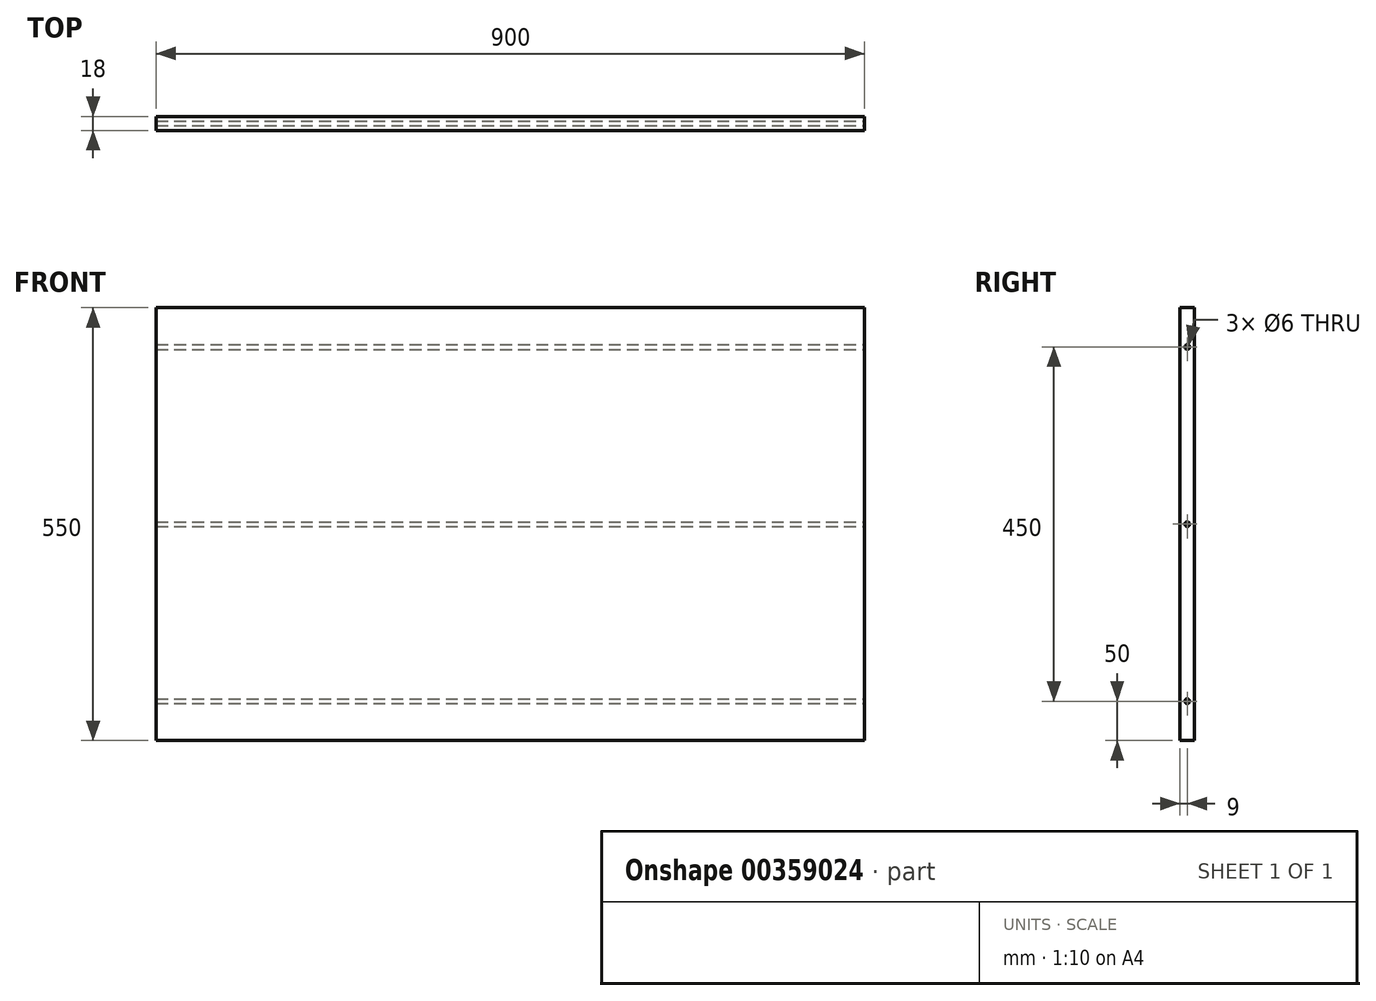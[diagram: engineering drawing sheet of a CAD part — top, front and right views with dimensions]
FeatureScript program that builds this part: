
annotation { "Feature Type Name" : "Feature", "Feature Type Description" : "" }
export const myFeature = defineFeature(function(context is Context, id is Id, definition is map)
    precondition{}
    {
        {
            var Q0;
            Q0=qCreatedBy(makeId("Front.planeOp"),FACE);
            var sketch = newSketch(context, id + "F0", { "sketchPlane" : qUnion([Q0])});
            skLineSegment(sketch, "E0.bottom", {"start": v(0, 0) * mm, "end": v(900, 0) * mm});
            skLineSegment(sketch, "E0.top", {"start": v(0, 550) * mm, "end": v(900, 550) * mm});
            skLineSegment(sketch, "E0.left", {"start": v(0, 0) * mm, "end": v(0, 550) * mm});
            skLineSegment(sketch, "E0.right", {"start": v(900, 0) * mm, "end": v(900, 550) * mm});
            skSolve(sketch);
        }
        {
            var Q0;
            Q0=makeQuery(id+"F0.imprint","IMPRINT",FACE,{"disambiguationData":[TD([[makeQuery(id+"F0.imprint","IMPRINT",EDGE,{"derivedFrom":sQuery(id+"F0.wireOp",EDGE,"E0.bottom")}),1.0]])]});
            extrude(context, id + "F1", {"entities" : qUnion([Q0]), "depth" : 18 * mm});
        }
        {
            var Q0;
            Q0=makeQuery(id+"F1.opExtrude","SWEPT_FACE",FACE,{"disambiguationData":[OSD([sQuery(id+"F0.wireOp",EDGE,"E0.right")])]});
            var sketch = newSketch(context, id + "F2", { "sketchPlane" : qUnion([Q0])});
            skLineSegment(sketch, "E1", {"start": v(-9, 558.74) * mm, "end": v(-9, -16.51) * mm, "construction": true});
            skCircle(sketch, "E2", {"center": v(-9, 50) * mm, "radius": 3 * mm});
            skCircle(sketch, "E3", {"center": v(-9, 275) * mm, "radius": 3 * mm});
            skCircle(sketch, "E4", {"center": v(-9, 500) * mm, "radius": 3 * mm});
            skSolve(sketch);
        }
        {
            var Q0;
            Q0 = qSketchRegion(id + "F2", true);
            extrude(context, id + "F3", {"entities" : qUnion([Q0]), "operationType" : NewBodyOperationType.REMOVE, "endBound" : BoundingType.THROUGH_ALL, "oppositeDirection" : true, "depth" : 15 * mm});
        }
    });
